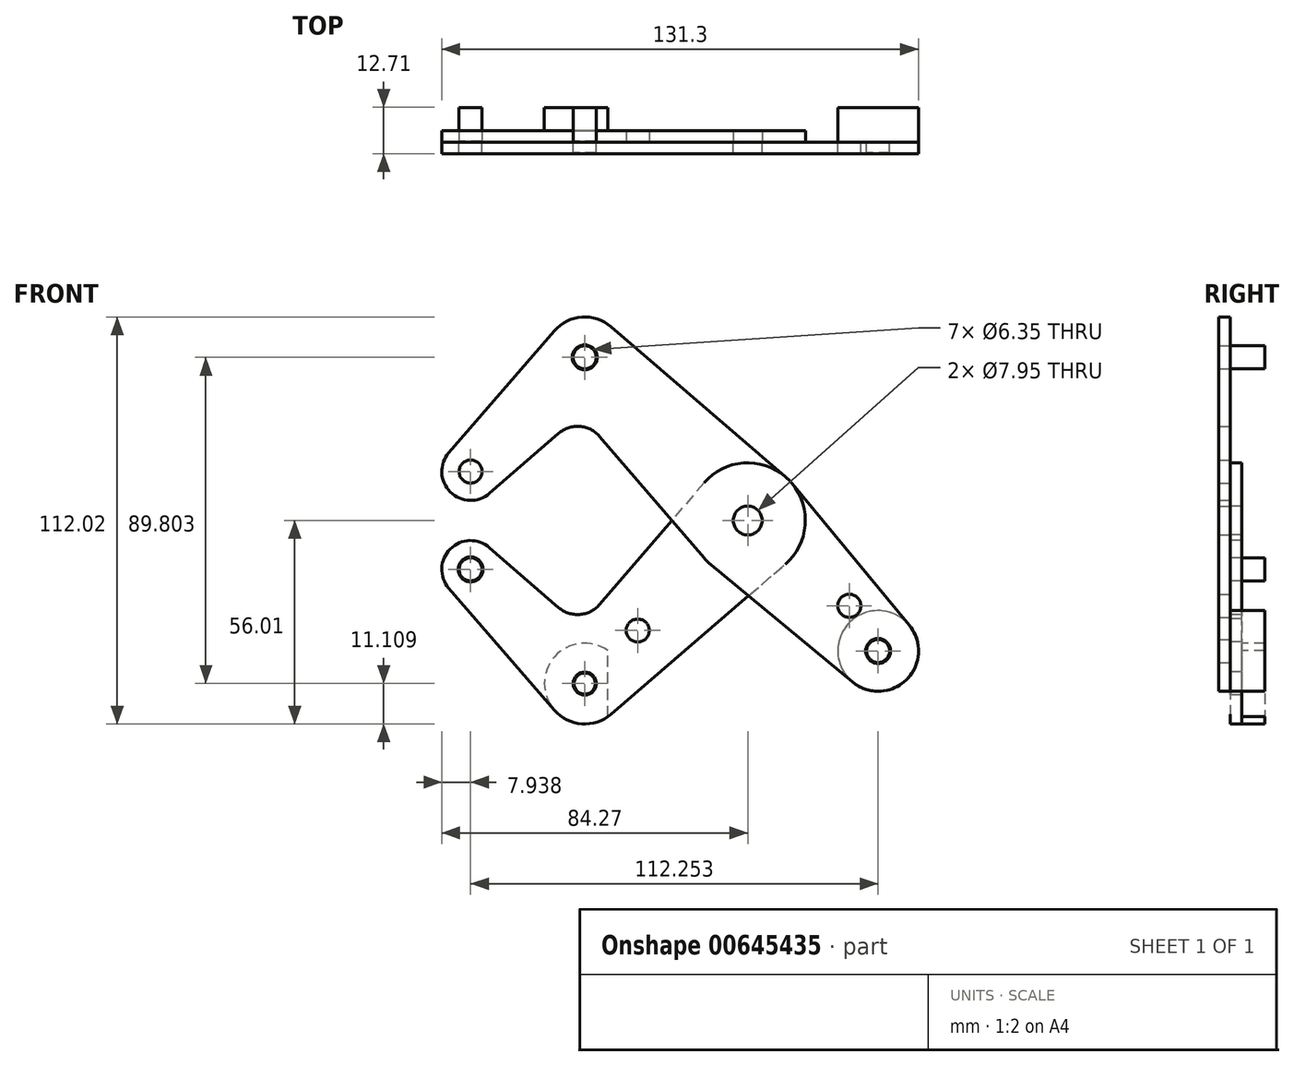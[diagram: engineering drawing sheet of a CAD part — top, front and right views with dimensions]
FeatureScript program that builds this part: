
annotation { "Feature Type Name" : "Feature", "Feature Type Description" : "" }
export const myFeature = defineFeature(function(context is Context, id is Id, definition is map)
    precondition{}
    {
        {
            var Q0;
            Q0=qCreatedBy(makeId("Front.planeOp"),FACE);
            var sketch = newSketch(context, id + "F0", { "sketchPlane" : qUnion([Q0])});
            skLineSegment(sketch, "E0", {"start": v(0, 0) * mm, "end": v(-44.9, 44.9) * mm});
            skLineSegment(sketch, "E1", {"start": v(-44.9, 44.9) * mm, "end": v(35.92, -35.92) * mm, "construction": true});
            skCircle(sketch, "E2", {"center": v(-44.9, 44.9) * mm, "radius": 3.18 * mm});
            skCircle(sketch, "E3", {"center": v(-44.9, 44.9) * mm, "radius": 11.11 * mm});
            skCircle(sketch, "E4", {"center": v(0, 0) * mm, "radius": 3.98 * mm});
            skCircle(sketch, "E5", {"center": v(0, 0) * mm, "radius": 15.88 * mm});
            skCircle(sketch, "E6", {"center": v(35.92, -35.92) * mm, "radius": 3.18 * mm});
            skLineSegment(sketch, "E7", {"start": v(-44.9, 44.9) * mm, "end": v(-76.33, 13.47) * mm, "construction": true});
            skLineSegment(sketch, "E8", {"start": v(-76.33, 13.47) * mm, "end": v(-76.33, -13.47) * mm, "construction": true});
            skLineSegment(sketch, "E9", {"start": v(-76.33, -13.47) * mm, "end": v(-44.9, -44.9) * mm, "construction": true});
            skLineSegment(sketch, "E10", {"start": v(-44.9, -44.9) * mm, "end": v(0, 0) * mm, "construction": true});
            skCircle(sketch, "E11", {"center": v(-76.33, 13.47) * mm, "radius": 3.18 * mm});
            skCircle(sketch, "E12", {"center": v(-76.33, 13.47) * mm, "radius": 7.94 * mm});
            skCircle(sketch, "E13", {"center": v(-76.33, -13.47) * mm, "radius": 3.18 * mm});
            skCircle(sketch, "E14", {"center": v(-76.33, -13.47) * mm, "radius": 7.94 * mm});
            skCircle(sketch, "E15", {"center": v(-44.9, -44.9) * mm, "radius": 3.18 * mm});
            skCircle(sketch, "E16", {"center": v(-44.9, -44.9) * mm, "radius": 11.11 * mm});
            skCircle(sketch, "E17", {"center": v(-30.3, -30.3) * mm, "radius": 3.18 * mm});
            skCircle(sketch, "E18", {"center": v(27.97, -23.48) * mm, "radius": 3.18 * mm});
            skCircle(sketch, "E19", {"center": v(0, 0) * mm, "radius": 3.18 * mm});
            skCircle(sketch, "E20", {"center": v(35.92, -35.92) * mm, "radius": 11.11 * mm});
            skLineSegment(sketch, "E21", {"start": v(12.23, 10.12) * mm, "end": v(44.48, -28.83) * mm});
            skLineSegment(sketch, "E22", {"start": v(-10.12, -12.23) * mm, "end": v(28.83, -44.48) * mm});
            skLineSegment(sketch, "E23", {"start": v(-37.66, 53.33) * mm, "end": v(10.35, 12.04) * mm});
            skLineSegment(sketch, "E24", {"start": v(-82.33, 18.67) * mm, "end": v(-53.3, 52.18) * mm});
            skLineSegment(sketch, "E25", {"start": v(-82.33, -18.67) * mm, "end": v(-53.3, -52.18) * mm});
            skLineSegment(sketch, "E26", {"start": v(-37.66, -53.33) * mm, "end": v(10.35, -12.04) * mm});
            skLineSegment(sketch, "E27", {"start": v(-12.04, 10.35) * mm, "end": v(-40.85, -23.15) * mm});
            skLineSegment(sketch, "E28", {"start": v(-71.13, -7.47) * mm, "end": v(-52.08, -23.98) * mm});
            skArc(sketch, "E29.filletArc", {"start": v(-52.08, -23.98) * mm, "mid": v(-46.3, -25.9) * mm, "end": v(-40.85, -23.15) * mm});
            skLineSegment(sketch, "E30", {"start": v(-71.13, 7.47) * mm, "end": v(-52.08, 23.98) * mm});
            skLineSegment(sketch, "E31", {"start": v(-40.85, 23.15) * mm, "end": v(-12.04, -10.35) * mm});
            skArc(sketch, "E32.filletArc", {"start": v(-40.85, 23.15) * mm, "mid": v(-46.3, 25.9) * mm, "end": v(-52.08, 23.98) * mm});
            skLineSegment(sketch, "E33", {"start": v(-38.55, -35.78) * mm, "end": v(-38.55, -54.02) * mm});
            skLineSegment(sketch, "E34", {"start": v(35.92, -35.92) * mm, "end": v(-38.55, -44.9) * mm, "construction": true});
            skSolve(sketch);
        }
        {
            var Q0;
            {var subQ0=sQuery(id+"F0.wireOp",EDGE,"E24");Q0=makeQuery(id+"F0.imprint","IMPRINT",FACE,{"disambiguationData":[TD([[makeQuery(id+"F0.imprint","IMPRINT",EDGE,{"derivedFrom":subQ0}),-1.0]])]});}
            var Q1;
            Q1=makeQuery(id+"F0.imprint","IMPRINT",FACE,{"disambiguationData":[TD([[makeQuery(id+"F0.imprint","IMPRINT",EDGE,{"derivedFrom":sQuery(id+"F0.wireOp",EDGE,"E2")}),-1.0]])]});
            var Q2;
            Q2=makeQuery(id+"F0.imprint","IMPRINT",FACE,{"disambiguationData":[TD([[makeQuery(id+"F0.imprint","IMPRINT",EDGE,{"derivedFrom":sQuery(id+"F0.wireOp",EDGE,"E11")}),-1.0]])]});
            var Q3;
            {var subQ5=sQuery(id+"F0.wireOp",EDGE,"E23");Q3=makeQuery(id+"F0.imprint","IMPRINT",FACE,{"disambiguationData":[TD([[makeQuery(id+"F0.imprint","IMPRINT",EDGE,{"derivedFrom":subQ5}),-1.0]])]});}
            var Q4;
            Q4=makeQuery(id+"F0.imprint","IMPRINT",FACE,{"disambiguationData":[TD([[makeQuery(id+"F0.imprint","IMPRINT",EDGE,{"derivedFrom":sQuery(id+"F0.wireOp",EDGE,"E4")}),-1.0]])]});
            var Q5;
            {var subQ0=sQuery(id+"F0.wireOp",EDGE,"E22");var subQ1=sQuery(id+"F0.wireOp",EDGE,"E5");var subQ2=makeQuery(id+"F0.imprint","INTERSECT",VERTEX,{"derivedFrom":[subQ1,subQ0]});Q5=makeQuery(id+"F0.imprint","IMPRINT",FACE,{"disambiguationData":[TD([[makeQuery(id+"F0.imprint","IMPRINT",EDGE,{"disambiguationData":[TD([[subQ2,-1.0]])],"derivedFrom":subQ1}),-1.0]])]});}
            var Q6;
            {var subQ0=sQuery(id+"F0.wireOp",EDGE,"E27");var subQ1=sQuery(id+"F0.wireOp",EDGE,"E5");var subQ2=makeQuery(id+"F0.imprint","INTERSECT",VERTEX,{"derivedFrom":[subQ1,subQ0]});Q6=makeQuery(id+"F0.imprint","IMPRINT",FACE,{"disambiguationData":[TD([[makeQuery(id+"F0.imprint","IMPRINT",EDGE,{"disambiguationData":[TD([[subQ2,-1.0]])],"derivedFrom":subQ1}),-1.0]])]});}
            var Q7;
            Q7=makeQuery(id+"F0.imprint","IMPRINT",FACE,{"disambiguationData":[TD([[makeQuery(id+"F0.imprint","IMPRINT",EDGE,{"derivedFrom":sQuery(id+"F0.wireOp",EDGE,"E18")}),-1.0]])]});
            var Q8;
            Q8=makeQuery(id+"F0.imprint","IMPRINT",FACE,{"disambiguationData":[TD([[makeQuery(id+"F0.imprint","IMPRINT",EDGE,{"derivedFrom":sQuery(id+"F0.wireOp",EDGE,"E6")}),-1.0]])]});
            extrude(context, id + "F1", {"entities" : qUnion([Q0, Q1, Q2, Q3, Q4, Q5, Q6, Q7, Q8]), "depth" : 3.17 * mm, "offsetDistance" : 25.4 * mm});
        }
        {
            var Q0;
            Q0=makeQuery(id+"F0.imprint","IMPRINT",FACE,{"disambiguationData":[TD([[makeQuery(id+"F0.imprint","IMPRINT",EDGE,{"derivedFrom":sQuery(id+"F0.wireOp",EDGE,"E13")}),-1.0]])]});
            var Q1;
            Q1=makeQuery(id+"F0.imprint","IMPRINT",FACE,{"disambiguationData":[TD([[makeQuery(id+"F0.imprint","IMPRINT",EDGE,{"derivedFrom":sQuery(id+"F0.wireOp",EDGE,"E17")}),-1.0]])]});
            var Q2;
            Q2=makeQuery(id+"F0.imprint","IMPRINT",FACE,{"disambiguationData":[TD([[makeQuery(id+"F0.imprint","IMPRINT",EDGE,{"derivedFrom":sQuery(id+"F0.wireOp",EDGE,"E15")}),-1.0]])]});
            var Q3;
            Q3=makeQuery(id+"F0.imprint","IMPRINT",FACE,{"disambiguationData":[TD([[makeQuery(id+"F0.imprint","IMPRINT",EDGE,{"derivedFrom":sQuery(id+"F0.wireOp",EDGE,"E4")}),-1.0]])]});
            var Q4;
            {var subQ0=sQuery(id+"F0.wireOp",EDGE,"E22");var subQ1=sQuery(id+"F0.wireOp",EDGE,"E5");var subQ2=makeQuery(id+"F0.imprint","INTERSECT",VERTEX,{"derivedFrom":[subQ1,subQ0]});Q4=makeQuery(id+"F0.imprint","IMPRINT",FACE,{"disambiguationData":[TD([[makeQuery(id+"F0.imprint","IMPRINT",EDGE,{"disambiguationData":[TD([[subQ2,-1.0]])],"derivedFrom":subQ1}),-1.0]])]});}
            var Q5;
            {var subQ0=sQuery(id+"F0.wireOp",EDGE,"E27");var subQ1=sQuery(id+"F0.wireOp",EDGE,"E5");var subQ2=makeQuery(id+"F0.imprint","INTERSECT",VERTEX,{"derivedFrom":[subQ1,subQ0]});Q5=makeQuery(id+"F0.imprint","IMPRINT",FACE,{"disambiguationData":[TD([[makeQuery(id+"F0.imprint","IMPRINT",EDGE,{"disambiguationData":[TD([[subQ2,-1.0]])],"derivedFrom":subQ1}),-1.0]])]});}
            var Q6;
            {var subQ2=sQuery(id+"F0.wireOp",EDGE,"E33");Q6=makeQuery(id+"F0.imprint","IMPRINT",FACE,{"disambiguationData":[TD([[makeQuery(id+"F0.imprint","IMPRINT",EDGE,{"derivedFrom":subQ2}),1.0]])]});}
            extrude(context, id + "F2", {"entities" : qUnion([Q0, Q1, Q2, Q3, Q4, Q5, Q6]), "oppositeDirection" : true, "depth" : 3.17 * mm, "offsetDistance" : 25.4 * mm});
        }
        {
            var Q0;
            Q0=qCreatedBy(makeId("Front.planeOp"),FACE);
            cPlane(context, id + "F3", {"entities" : qUnion([Q0]), "cplaneType" : CPlaneType.OFFSET, "offset" : 9.52 * mm, "oppositeDirection" : true, "width" : 152.4 * mm, "height" : 152.4 * mm});
        }
        {
            var Q0;
            Q0=makeQuery(id+"F0.imprint","IMPRINT",FACE,{"disambiguationData":[TD([[makeQuery(id+"F0.imprint","IMPRINT",EDGE,{"derivedFrom":sQuery(id+"F0.wireOp",EDGE,"E15")}),-1.0]])]});
            var Q1;
            Q1=makeQuery(id+"F0.imprint","IMPRINT",FACE,{"disambiguationData":[TD([[makeQuery(id+"F0.imprint","IMPRINT",EDGE,{"derivedFrom":sQuery(id+"F0.wireOp",EDGE,"E6")}),-1.0]])]});
            var Q2;
            Q2=makeQuery(id+"F0.imprint","IMPRINT",FACE,{"disambiguationData":[TD([[makeQuery(id+"F0.imprint","IMPRINT",EDGE,{"derivedFrom":sQuery(id+"F0.wireOp",EDGE,"E2")}),1.0]])]});
            var Q3;
            Q3=makeQuery(id+"F0.imprint","IMPRINT",FACE,{"disambiguationData":[TD([[makeQuery(id+"F0.imprint","IMPRINT",EDGE,{"derivedFrom":sQuery(id+"F0.wireOp",EDGE,"E13")}),1.0]])]});
            var Q4;
            Q4=makeQuery(id+"F0.imprint","IMPRINT",FACE,{"disambiguationData":[TD([[makeQuery(id+"F0.imprint","IMPRINT",EDGE,{"derivedFrom":sQuery(id+"F0.wireOp",EDGE,"E6")}),1.0]])]});
            var Q5;
            Q5=makeQuery(id+"F0.imprint","IMPRINT",FACE,{"disambiguationData":[TD([[makeQuery(id+"F0.imprint","IMPRINT",EDGE,{"derivedFrom":sQuery(id+"F0.wireOp",EDGE,"E15")}),1.0]])]});
            var Q6;
            Q6=qCreatedBy(id+"F3.planeOp",FACE);
            extrude(context, id + "F4", {"entities" : qUnion([Q0, Q1, Q2, Q3, Q4, Q5]), "endBound" : BoundingType.UP_TO_SURFACE, "oppositeDirection" : true, "depth" : 25.4 * mm, "endBoundEntityFace" : qUnion([Q6]), "offsetDistance" : 25.4 * mm});
        }
        {
            var Q0;
            Q0=makeQuery(id+"F1.opExtrude","SWEPT_BODY",BODY,{"disambiguationData":[OSD([sQuery(id+"F0.wireOp",EDGE,"E2"),sQuery(id+"F0.wireOp",EDGE,"E3"),sQuery(id+"F0.wireOp",EDGE,"E4"),sQuery(id+"F0.wireOp",EDGE,"E5"),sQuery(id+"F0.wireOp",EDGE,"E6"),sQuery(id+"F0.wireOp",EDGE,"E11"),sQuery(id+"F0.wireOp",EDGE,"E12"),sQuery(id+"F0.wireOp",EDGE,"E18"),sQuery(id+"F0.wireOp",EDGE,"E20"),sQuery(id+"F0.wireOp",EDGE,"E21"),sQuery(id+"F0.wireOp",EDGE,"E22"),sQuery(id+"F0.wireOp",EDGE,"E23"),sQuery(id+"F0.wireOp",EDGE,"E24"),sQuery(id+"F0.wireOp",EDGE,"E30"),sQuery(id+"F0.wireOp",EDGE,"E31"),sQuery(id+"F0.wireOp",EDGE,"E32.filletArc")])]});
            var Q1;
            Q1=makeQuery(id+"F2.opExtrude","SWEPT_BODY",BODY,{"disambiguationData":[OSD([sQuery(id+"F0.wireOp",EDGE,"E4"),sQuery(id+"F0.wireOp",EDGE,"E5"),sQuery(id+"F0.wireOp",EDGE,"E13"),sQuery(id+"F0.wireOp",EDGE,"E14"),sQuery(id+"F0.wireOp",EDGE,"E15"),sQuery(id+"F0.wireOp",EDGE,"E16"),sQuery(id+"F0.wireOp",EDGE,"E17"),sQuery(id+"F0.wireOp",EDGE,"E25"),sQuery(id+"F0.wireOp",EDGE,"E26"),sQuery(id+"F0.wireOp",EDGE,"E27"),sQuery(id+"F0.wireOp",EDGE,"E28"),sQuery(id+"F0.wireOp",EDGE,"E29.filletArc")])]});
            var Q2;
            Q2=makeQuery(id+"F4.opExtrude","SWEPT_BODY",BODY,{"disambiguationData":[OSD([sQuery(id+"F0.wireOp",EDGE,"E2")])]});
            var Q3;
            Q3=makeQuery(id+"F4.opExtrude","SWEPT_BODY",BODY,{"disambiguationData":[OSD([sQuery(id+"F0.wireOp",EDGE,"E20")])]});
            var Q4;
            Q4=makeQuery(id+"F4.opExtrude","SWEPT_BODY",BODY,{"disambiguationData":[OSD([sQuery(id+"F0.wireOp",EDGE,"E16"),sQuery(id+"F0.wireOp",EDGE,"E33")])]});
            var Q5;
            Q5=makeQuery(id+"F4.opExtrude","SWEPT_BODY",BODY,{"disambiguationData":[OSD([sQuery(id+"F0.wireOp",EDGE,"E13")])]});
            booleanBodies(context, id + "F5", {"operationType" : BooleanOperationType.SUBTRACTION, "tools" : qUnion([Q0, Q1]), "targets" : qUnion([Q2, Q3, Q4, Q5]), "keepTools" : true});
        }
        {
            var Q0;
            Q0=makeQuery(id+"F4.opExtrude","CAP_FACE",FACE,{"disambiguationData":[OSD([sQuery(id+"F0.wireOp",EDGE,"E16"),sQuery(id+"F0.wireOp",EDGE,"E33")])],"isStart":true});
            var Q1;
            Q1=makeQuery(id+"F2.opExtrude","CAP_EDGE",EDGE,{"disambiguationData":[OSD([sQuery(id+"F0.wireOp",EDGE,"E13")])],"isStart":true});
            var Q2;
            Q2=makeQuery(id+"F1.opExtrude","CAP_EDGE",EDGE,{"disambiguationData":[OSD([sQuery(id+"F0.wireOp",EDGE,"E2")])],"isStart":false});
            var Q3;
            Q3=makeQuery(id+"F1.opExtrude","CAP_EDGE",EDGE,{"disambiguationData":[OSD([sQuery(id+"F0.wireOp",EDGE,"E6")])],"isStart":false});
            chamfer(context, id + "F6", {"entities" : qUnion([Q0, Q1, Q2, Q3]), "width" : 0.25 * mm, "tangentPropagation" : true});
        }
    });
